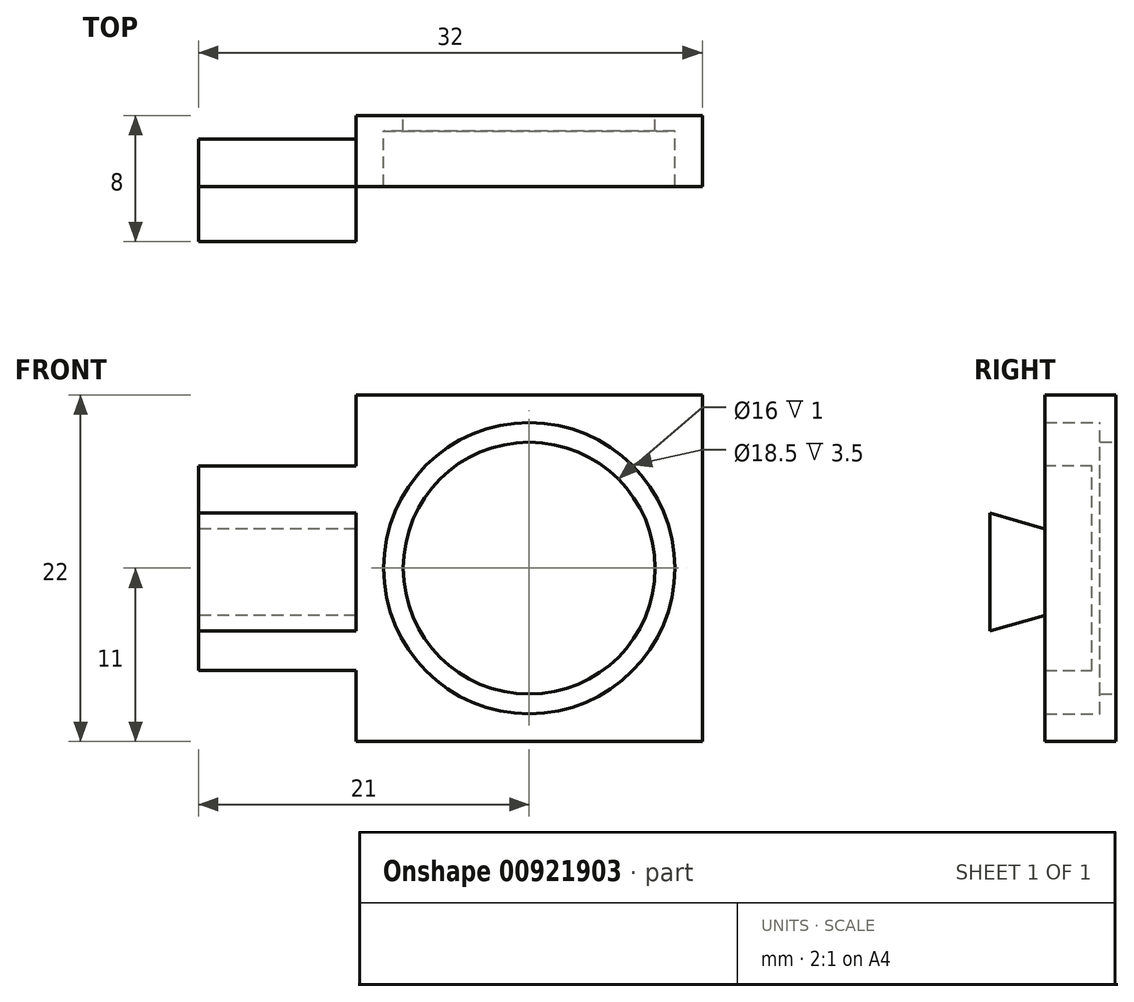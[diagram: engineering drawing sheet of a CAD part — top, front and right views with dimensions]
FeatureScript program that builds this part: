
annotation { "Feature Type Name" : "Feature", "Feature Type Description" : "" }
export const myFeature = defineFeature(function(context is Context, id is Id, definition is map)
    precondition{}
    {
        {
            var Q0;
            Q0=qCreatedBy(makeId("Front.planeOp"),FACE);
            var sketch = newSketch(context, id + "F0", { "sketchPlane" : qUnion([Q0])});
            skLineSegment(sketch, "E0.bottom", {"start": v(0, 0) * mm, "end": v(22, 0) * mm});
            skLineSegment(sketch, "E0.top", {"start": v(0, 22) * mm, "end": v(22, 22) * mm});
            skLineSegment(sketch, "E0.left", {"start": v(0, 0) * mm, "end": v(0, 22) * mm});
            skLineSegment(sketch, "E0.right", {"start": v(22, 0) * mm, "end": v(22, 22) * mm});
            skCircle(sketch, "E1", {"center": v(11, 11) * mm, "radius": 8 * mm});
            skSolve(sketch);
        }
        {
            var Q0;
            Q0=makeQuery(id+"F0.imprint","IMPRINT",FACE,{"disambiguationData":[TD([[makeQuery(id+"F0.imprint","IMPRINT",EDGE,{"derivedFrom":sQuery(id+"F0.wireOp",EDGE,"E0.bottom")}),1.0]])]});
            extrude(context, id + "F1", {"entities" : qUnion([Q0]), "depth" : 1 * mm, "offsetDistance" : 25 * mm});
        }
        {
            var Q0;
            Q0=makeQuery(id+"F1.opExtrude","CAP_FACE",FACE,{"disambiguationData":[OSD([sQuery(id+"F0.wireOp",EDGE,"E0.bottom"),sQuery(id+"F0.wireOp",EDGE,"E0.top"),sQuery(id+"F0.wireOp",EDGE,"E0.left"),sQuery(id+"F0.wireOp",EDGE,"E0.right"),sQuery(id+"F0.wireOp",EDGE,"E1")])],"isStart":false});
            var sketch = newSketch(context, id + "F2", { "sketchPlane" : qUnion([Q0])});
            skCircle(sketch, "E2", {"center": v(11, 11) * mm, "radius": 9.25 * mm});
            skSolve(sketch);
        }
        {
            var Q0;
            Q0=makeQuery(id+"F2.imprint","IMPRINT",FACE,{"disambiguationData":[TD([[makeQuery(id+"F2.imprint","IMPRINT",EDGE,{"derivedFrom":sQuery(id+"F2.wireOp",EDGE,"E2")}),-1.0]])]});
            extrude(context, id + "F3", {"entities" : qUnion([Q0]), "operationType" : NewBodyOperationType.ADD, "depth" : 3.5 * mm, "offsetDistance" : 25 * mm});
        }
        {
            var Q0;
            {var subQ0=sQuery(id+"F0.wireOp",EDGE,"E0.left");Q0=makeQuery(id+"F3.boolean.opBoolean","MERGE",FACE,{"derivedFrom":[makeQuery(id+"F1.opExtrude","SWEPT_FACE",FACE,{"disambiguationData":[OSD([subQ0])]}),makeQuery(id+"F3.opExtrude","SWEPT_FACE",FACE,{"disambiguationData":[OSD([subQ0])]})]});}
            var sketch = newSketch(context, id + "F4", { "sketchPlane" : qUnion([Q0])});
            skLineSegment(sketch, "E3", {"start": v(4.5, 4.5) * mm, "end": v(1.5, 4.5) * mm});
            skLineSegment(sketch, "E4", {"start": v(1.5, 4.5) * mm, "end": v(1.5, 17.5) * mm});
            skLineSegment(sketch, "E5", {"start": v(1.5, 17.5) * mm, "end": v(4.5, 17.5) * mm});
            skSolve(sketch);
        }
        {
            var Q0;
            {var subQ0=sQuery(id+"F4.wireOp",EDGE,"E3");Q0=makeQuery(id+"F4.imprint","IMPRINT",FACE,{"disambiguationData":[TD([[makeQuery(id+"F4.imprint","IMPRINT",EDGE,{"derivedFrom":subQ0}),-1.0]])]});}
            extrude(context, id + "F5", {"entities" : qUnion([Q0]), "operationType" : NewBodyOperationType.ADD, "depth" : 10 * mm, "offsetDistance" : 25 * mm});
        }
        {
            var Q0;
            {var subQ0=sQuery(id+"F0.wireOp",EDGE,"E0.left");Q0=makeQuery(id+"F5.boolean.opBoolean","MERGE",FACE,{"derivedFrom":[makeQuery(id+"F3.opExtrude","CAP_FACE",FACE,{"disambiguationData":[OSD([sQuery(id+"F0.wireOp",EDGE,"E0.bottom"),sQuery(id+"F0.wireOp",EDGE,"E0.top"),subQ0,sQuery(id+"F0.wireOp",EDGE,"E0.right"),sQuery(id+"F2.wireOp",EDGE,"E2")])],"isStart":false}),makeQuery(id+"F5.opExtrude","SWEPT_FACE",FACE,{"disambiguationData":[OSD([subQ0])]})]});}
            var sketch = newSketch(context, id + "F6", { "sketchPlane" : qUnion([Q0])});
            skLineSegment(sketch, "E6", {"start": v(-10, 14.5) * mm, "end": v(0, 14.5) * mm});
            skLineSegment(sketch, "E7", {"start": v(0, 14.5) * mm, "end": v(0, 7) * mm});
            skLineSegment(sketch, "E8", {"start": v(0, 7) * mm, "end": v(-10, 7) * mm});
            skSolve(sketch);
        }
        {
            var Q0;
            {var subQ0=sQuery(id+"F6.wireOp",EDGE,"E6");Q0=makeQuery(id+"F6.imprint","IMPRINT",FACE,{"disambiguationData":[TD([[makeQuery(id+"F6.imprint","IMPRINT",EDGE,{"derivedFrom":subQ0}),-1.0]])]});}
            extrude(context, id + "F7", {"entities" : qUnion([Q0]), "operationType" : NewBodyOperationType.ADD, "depth" : 3.5 * mm, "offsetDistance" : 25 * mm});
        }
        {
            var Q0;
            {var subQ0=sQuery(id+"F0.wireOp",EDGE,"E0.left");Q0=makeQuery(id+"F7.boolean.opBoolean","MERGE",FACE,{"derivedFrom":[makeQuery(id+"F5.opExtrude","CAP_FACE",FACE,{"disambiguationData":[OSD([subQ0,sQuery(id+"F4.wireOp",EDGE,"E3"),sQuery(id+"F4.wireOp",EDGE,"E4"),sQuery(id+"F4.wireOp",EDGE,"E5")])],"isStart":false}),makeQuery(id+"F7.opExtrude","SWEPT_FACE",FACE,{"disambiguationData":[OSD([subQ0])]})]});}
            var sketch = newSketch(context, id + "F8", { "sketchPlane" : qUnion([Q0])});
            skLineSegment(sketch, "E9", {"start": v(8, 14.5) * mm, "end": v(4.5, 13.5) * mm});
            skLineSegment(sketch, "E10", {"start": v(4.5, 13.5) * mm, "end": v(4.5, 14.5) * mm});
            skLineSegment(sketch, "E11", {"start": v(8, 7) * mm, "end": v(4.5, 8) * mm});
            skLineSegment(sketch, "E12", {"start": v(4.5, 8) * mm, "end": v(4.5, 7) * mm});
            skSolve(sketch);
        }
        {
            var Q0;
            Q0=makeQuery(id+"F8.imprint","IMPRINT",FACE,{"disambiguationData":[TD([[makeQuery(id+"F8.imprint","IMPRINT",EDGE,{"derivedFrom":sQuery(id+"F8.wireOp",EDGE,"E11")}),1.0]])]});
            extrude(context, id + "F9", {"entities" : qUnion([Q0]), "operationType" : NewBodyOperationType.REMOVE, "oppositeDirection" : true, "depth" : 10 * mm, "offsetDistance" : 25 * mm});
        }
        {
            var Q0;
            Q0=makeQuery(id+"F8.imprint","IMPRINT",FACE,{"disambiguationData":[TD([[makeQuery(id+"F8.imprint","IMPRINT",EDGE,{"derivedFrom":sQuery(id+"F8.wireOp",EDGE,"E9")}),-1.0]])]});
            extrude(context, id + "F10", {"entities" : qUnion([Q0]), "operationType" : NewBodyOperationType.REMOVE, "oppositeDirection" : true, "depth" : 10 * mm, "offsetDistance" : 25 * mm});
        }
    });
